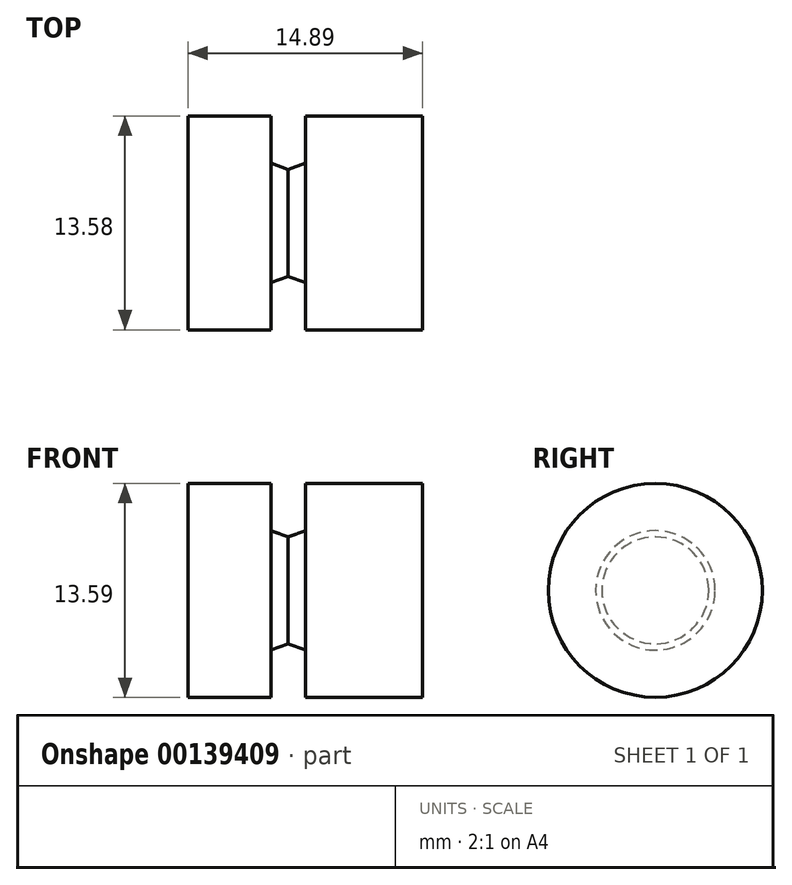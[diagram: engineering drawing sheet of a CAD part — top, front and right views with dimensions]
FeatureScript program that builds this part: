
annotation { "Feature Type Name" : "Feature", "Feature Type Description" : "" }
export const myFeature = defineFeature(function(context is Context, id is Id, definition is map)
    precondition{}
    {
        {
            var Q0;
            Q0=qCreatedBy(makeId("Front.planeOp"),FACE);
            var sketch = newSketch(context, id + "F0", { "sketchPlane" : qUnion([Q0])});
            skLineSegment(sketch, "E0", {"start": v(-1.1, 3) * mm, "end": v(-1.1, 0) * mm});
            skLineSegment(sketch, "E1", {"start": v(-1.1, 0) * mm, "end": v(0, -0.4) * mm});
            skLineSegment(sketch, "E2", {"start": v(0, -0.4) * mm, "end": v(1.1, 0) * mm});
            skLineSegment(sketch, "E3", {"start": v(1.1, 0) * mm, "end": v(1.1, 2.83) * mm});
            skLineSegment(sketch, "E4", {"start": v(1.1, 3) * mm, "end": v(1.1, 2.83) * mm});
            skLineSegment(sketch, "E5", {"start": v(-1.1, 3) * mm, "end": v(-6.36, 3) * mm});
            skLineSegment(sketch, "E6", {"start": v(1.1, 3) * mm, "end": v(8.53, 3) * mm});
            skLineSegment(sketch, "E7", {"start": v(-6.36, 3) * mm, "end": v(-6.36, -3.8) * mm});
            skLineSegment(sketch, "E8", {"start": v(-6.36, -3.8) * mm, "end": v(8.53, -3.8) * mm});
            skLineSegment(sketch, "E9", {"start": v(8.53, -3.8) * mm, "end": v(8.53, 3) * mm});
            skSolve(sketch);
        }
        {
            var Q0;
            Q0=makeQuery(id+"F0.imprint","IMPRINT",FACE,{"disambiguationData":[TD([[makeQuery(id+"F0.imprint","IMPRINT",EDGE,{"derivedFrom":sQuery(id+"F0.wireOp",EDGE,"E0")}),-1.0]])]});
            var Q1;
            Q1=sQuery(id+"F0.wireOp",EDGE,"E8");
            revolve(context, id + "F1", {"entities" : qUnion([Q0]), "axis" : qUnion([Q1]), "revolveType" : RevolveType.FULL});
        }
    });
